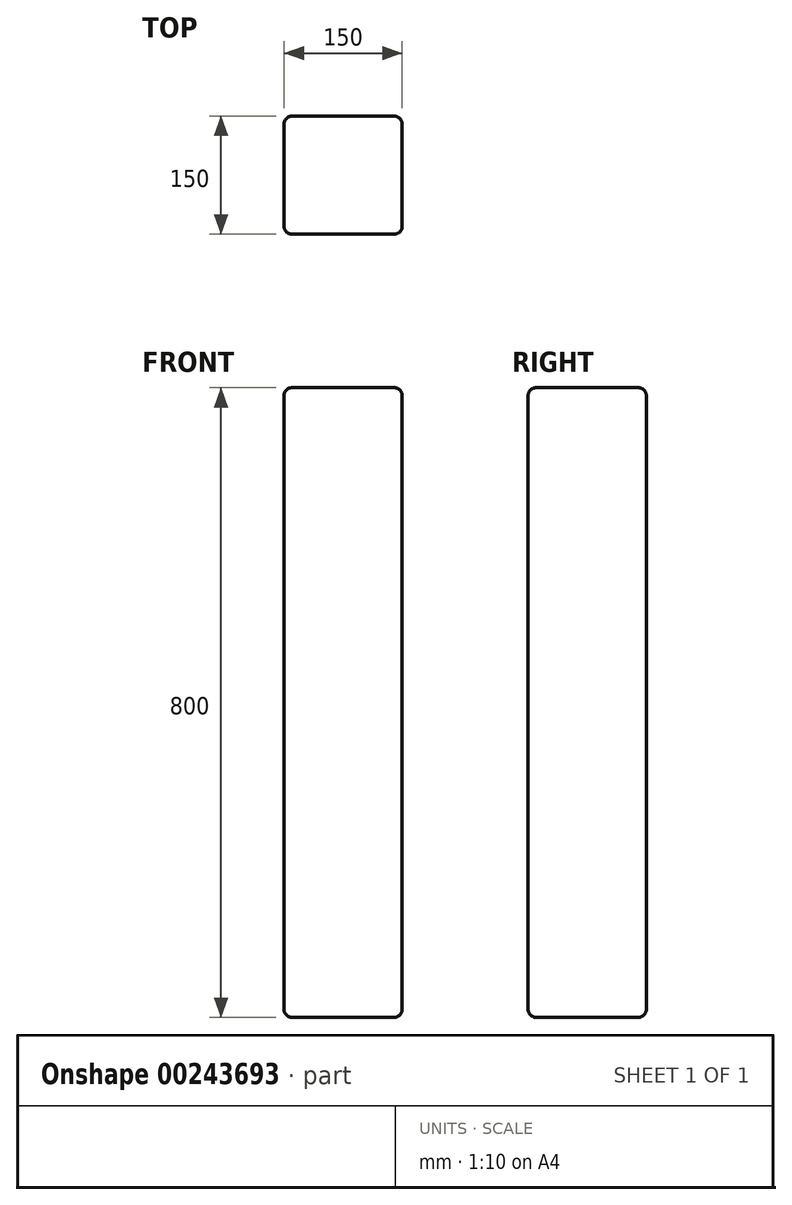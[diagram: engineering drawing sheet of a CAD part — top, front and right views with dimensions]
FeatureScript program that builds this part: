
annotation { "Feature Type Name" : "Feature", "Feature Type Description" : "" }
export const myFeature = defineFeature(function(context is Context, id is Id, definition is map)
    precondition{}
    {
        {
            var Q0;
            Q0=qCreatedBy(makeId("Front.planeOp"),FACE);
            var sketch = newSketch(context, id + "F0", { "sketchPlane" : qUnion([Q0])});
            skLineSegment(sketch, "E0.bottom", {"start": v(-75, 400) * mm, "end": v(75, 400) * mm});
            skLineSegment(sketch, "E0.top", {"start": v(-75, -400) * mm, "end": v(75, -400) * mm});
            skLineSegment(sketch, "E0.left", {"start": v(-75, 400) * mm, "end": v(-75, -400) * mm});
            skLineSegment(sketch, "E0.right", {"start": v(75, 400) * mm, "end": v(75, -400) * mm});
            skLineSegment(sketch, "E1", {"start": v(0, 400) * mm, "end": v(0, -400) * mm, "construction": true});
            skLineSegment(sketch, "E2", {"start": v(-75, 0) * mm, "end": v(75, 0) * mm, "construction": true});
            skSolve(sketch);
        }
        {
            var Q0;
            Q0=makeQuery(id+"F0.imprint","IMPRINT",FACE,{"disambiguationData":[TD([[makeQuery(id+"F0.imprint","IMPRINT",EDGE,{"derivedFrom":sQuery(id+"F0.wireOp",EDGE,"E0.bottom")}),-1.0]])]});
            extrude(context, id + "F1", {"entities" : qUnion([Q0]), "endBound" : BoundingType.SYMMETRIC, "depth" : 150 * mm});
        }
        {
            var Q0;
            Q0=makeQuery(id+"F1.opExtrude","CAP_EDGE",EDGE,{"disambiguationData":[OSD([sQuery(id+"F0.wireOp",EDGE,"E0.left")])],"isStart":false});
            var Q1;
            Q1=makeQuery(id+"F1.opExtrude","CAP_EDGE",EDGE,{"disambiguationData":[OSD([sQuery(id+"F0.wireOp",EDGE,"E0.right")])],"isStart":false});
            var Q2;
            Q2=makeQuery(id+"F1.opExtrude","CAP_EDGE",EDGE,{"disambiguationData":[OSD([sQuery(id+"F0.wireOp",EDGE,"E0.left")])],"isStart":true});
            var Q3;
            Q3=makeQuery(id+"F1.opExtrude","CAP_EDGE",EDGE,{"disambiguationData":[OSD([sQuery(id+"F0.wireOp",EDGE,"E0.right")])],"isStart":true});
            var Q4;
            Q4=makeQuery(id+"F1.opExtrude","SWEPT_EDGE",EDGE,{"disambiguationData":[OSD([sQuery(id+"F0.wireOp",EDGE,"E0.top"),sQuery(id+"F0.wireOp",EDGE,"E0.left")])]});
            var Q5;
            Q5=makeQuery(id+"F1.opExtrude","CAP_EDGE",EDGE,{"disambiguationData":[OSD([sQuery(id+"F0.wireOp",EDGE,"E0.top")])],"isStart":true});
            var Q6;
            Q6=makeQuery(id+"F1.opExtrude","SWEPT_EDGE",EDGE,{"disambiguationData":[OSD([sQuery(id+"F0.wireOp",EDGE,"E0.top"),sQuery(id+"F0.wireOp",EDGE,"E0.right")])]});
            var Q7;
            Q7=makeQuery(id+"F1.opExtrude","CAP_EDGE",EDGE,{"disambiguationData":[OSD([sQuery(id+"F0.wireOp",EDGE,"E0.top")])],"isStart":false});
            var Q8;
            Q8=makeQuery(id+"F1.opExtrude","CAP_EDGE",EDGE,{"disambiguationData":[OSD([sQuery(id+"F0.wireOp",EDGE,"E0.bottom")])],"isStart":true});
            var Q9;
            Q9=makeQuery(id+"F1.opExtrude","SWEPT_EDGE",EDGE,{"disambiguationData":[OSD([sQuery(id+"F0.wireOp",EDGE,"E0.bottom"),sQuery(id+"F0.wireOp",EDGE,"E0.left")])]});
            var Q10;
            Q10=makeQuery(id+"F1.opExtrude","CAP_EDGE",EDGE,{"disambiguationData":[OSD([sQuery(id+"F0.wireOp",EDGE,"E0.bottom")])],"isStart":false});
            var Q11;
            Q11=makeQuery(id+"F1.opExtrude","SWEPT_EDGE",EDGE,{"disambiguationData":[OSD([sQuery(id+"F0.wireOp",EDGE,"E0.bottom"),sQuery(id+"F0.wireOp",EDGE,"E0.right")])]});
            fillet(context, id + "F2", {"entities" : qUnion([Q0, Q1, Q2, Q3, Q4, Q5, Q6, Q7, Q8, Q9, Q10, Q11]), "radius" : 10 * mm, "tangentPropagation" : true, "allowEdgeOverflow" : false});
        }
    });
